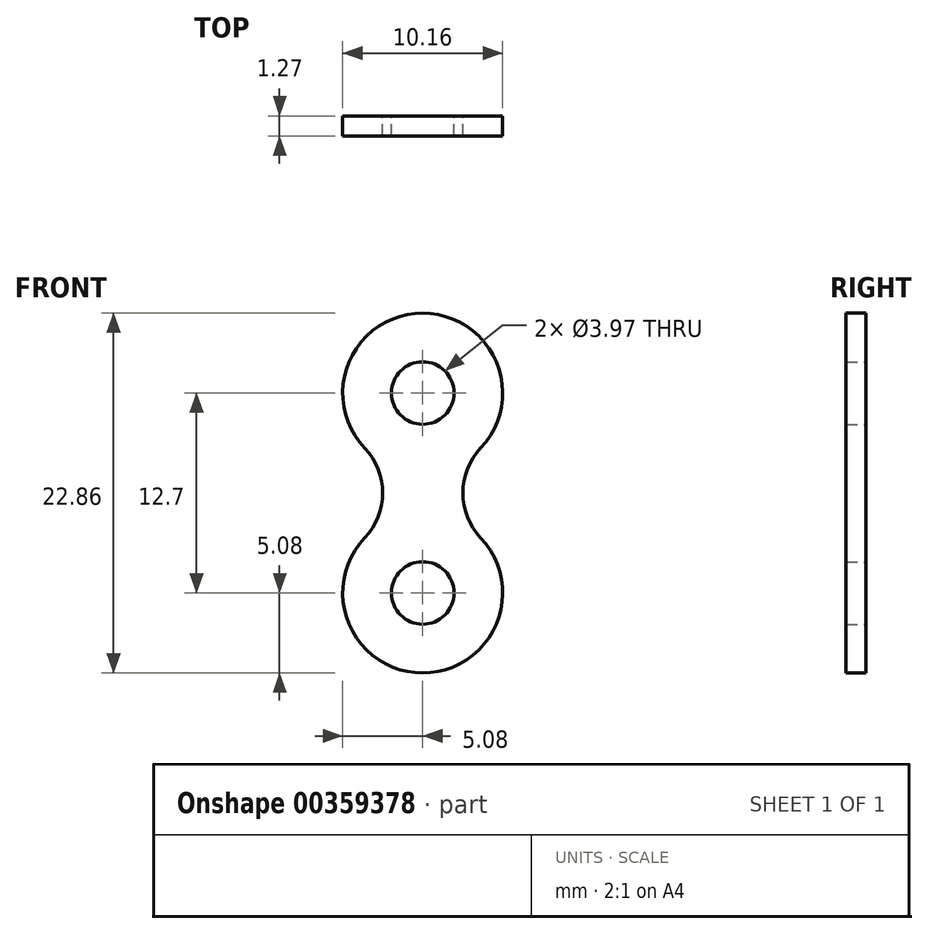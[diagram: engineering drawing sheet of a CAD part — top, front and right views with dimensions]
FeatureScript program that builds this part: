
annotation { "Feature Type Name" : "Feature", "Feature Type Description" : "" }
export const myFeature = defineFeature(function(context is Context, id is Id, definition is map)
    precondition{}
    {
        {
            var Q0;
            Q0=qCreatedBy(makeId("Front.planeOp"),FACE);
            var sketch = newSketch(context, id + "F0", { "sketchPlane" : qUnion([Q0])});
            skArc(sketch, "E0", {"start": v(3.69, -3.5) * mm, "mid": v(0, 5.08) * mm, "end": v(-3.69, -3.5) * mm});
            skArc(sketch, "E1", {"start": v(-3.69, -9.2) * mm, "mid": v(0, -17.78) * mm, "end": v(3.69, -9.2) * mm});
            skArc(sketch, "E2", {"start": v(-3.69, -9.2) * mm, "mid": v(-2.55, -6.35) * mm, "end": v(-3.69, -3.5) * mm});
            skArc(sketch, "E3", {"start": v(3.69, -3.5) * mm, "mid": v(2.55, -6.35) * mm, "end": v(3.69, -9.2) * mm});
            skCircle(sketch, "E4", {"center": v(0, 0) * mm, "radius": 1.98 * mm});
            skCircle(sketch, "E5", {"center": v(0, -12.7) * mm, "radius": 1.98 * mm});
            skSolve(sketch);
        }
        {
            var Q0;
            Q0=makeQuery(id+"F0.imprint","IMPRINT",FACE,{"disambiguationData":[TD([[makeQuery(id+"F0.imprint","IMPRINT",EDGE,{"derivedFrom":sQuery(id+"F0.wireOp",EDGE,"E0")}),1.0]])]});
            extrude(context, id + "F1", {"entities" : qUnion([Q0]), "depth" : 1.27 * mm});
        }
    });
